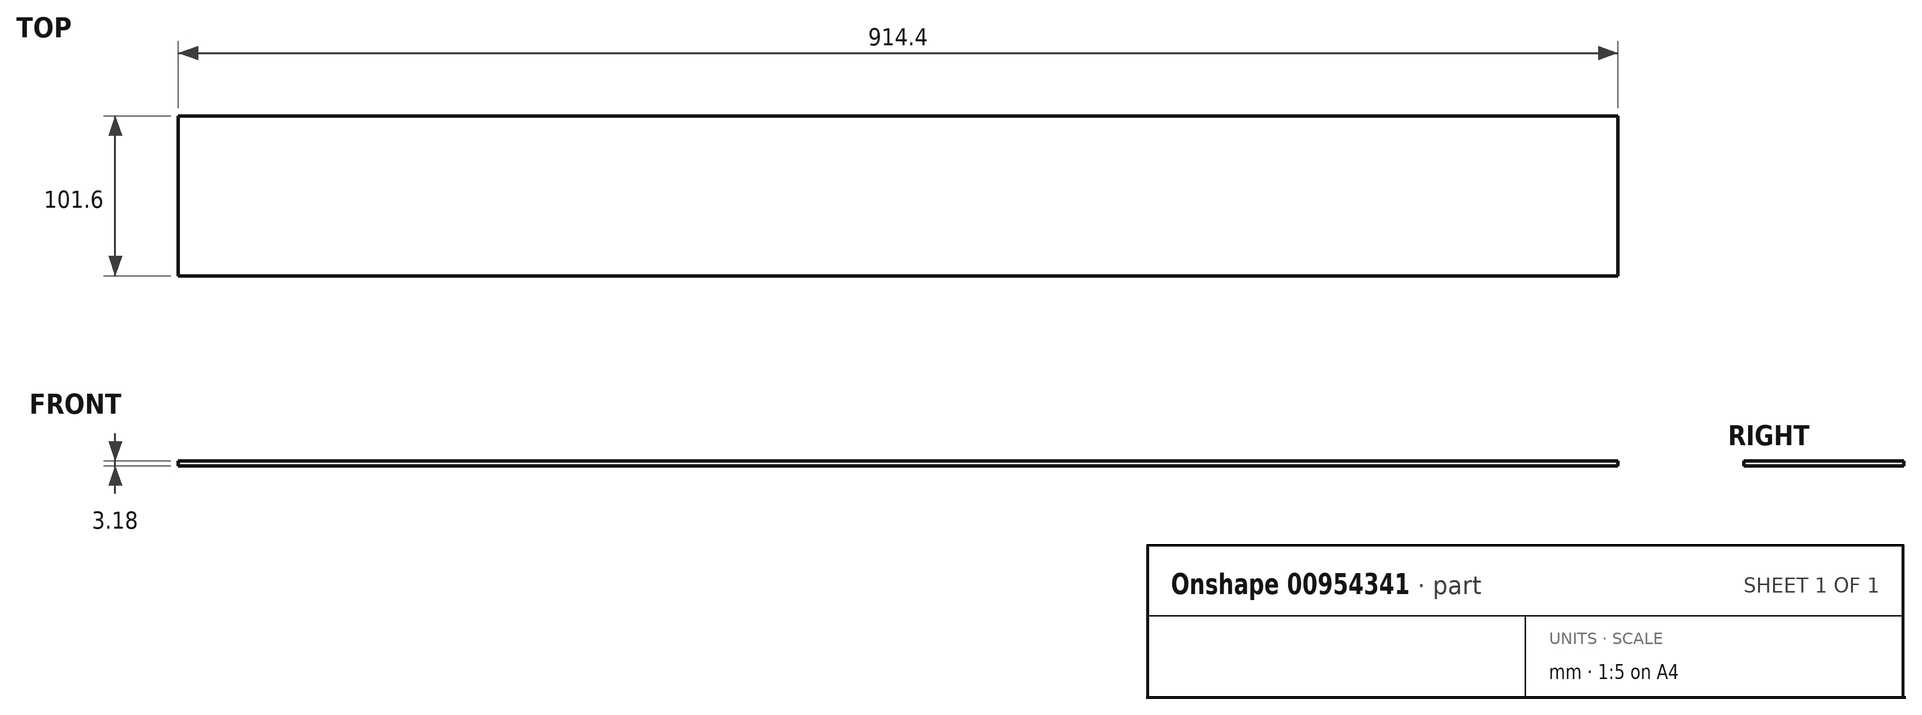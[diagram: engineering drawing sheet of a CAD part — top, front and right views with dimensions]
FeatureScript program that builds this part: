
annotation { "Feature Type Name" : "Feature", "Feature Type Description" : "" }
export const myFeature = defineFeature(function(context is Context, id is Id, definition is map)
    precondition{}
    {
        {
            var Q0;
            Q0=qCreatedBy(makeId("Top.planeOp"),FACE);
            var sketch = newSketch(context, id + "F0", { "sketchPlane" : qUnion([Q0])});
            skLineSegment(sketch, "E0.bottom", {"start": v(-42.9, -60.78) * mm, "end": v(871.5, -60.78) * mm});
            skLineSegment(sketch, "E0.top", {"start": v(-42.9, 40.82) * mm, "end": v(871.5, 40.82) * mm});
            skLineSegment(sketch, "E0.left", {"start": v(-42.9, -60.78) * mm, "end": v(-42.9, 40.82) * mm});
            skLineSegment(sketch, "E0.right", {"start": v(871.5, -60.78) * mm, "end": v(871.5, 40.82) * mm});
            skSolve(sketch);
        }
        {
            var Q0;
            Q0 = qSketchRegion(id + "F0", true);
            extrude(context, id + "F1", {"entities" : qUnion([Q0]), "depth" : 3.17 * mm, "offsetDistance" : 25.4 * mm, "symmetric" : true});
        }
    });
